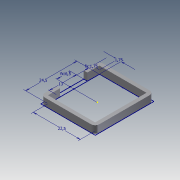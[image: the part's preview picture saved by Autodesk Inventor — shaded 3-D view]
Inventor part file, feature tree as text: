
AUTODESK INVENTOR PART (.ipt)
format: ipt  version: 2011 (Build 150239000, 239)  size: 93,696 bytes
history: native  units: mm
features: extrude x1, fillet x1, sketch x1
ambient origin geometry x8: Origin, YZ Plane, XZ Plane, XY Plane, X Axis, Y Axis, Z Axis, Center Point
bodies: Solid1 (feature_tree)
feature tree (3):
  extrude  "Extrusion1"  Depth=1.75mm
  fillet  "Fillet1"  Radius=24.5mm
  sketch  "Sketch1"  dims[d0=1.75mm d1=1.75mm d2=24.5mm d3=22.5mm d4=13.0mm d5=6.5mm d6=3.5mm d7=0.0mm d8=2.0mm]
